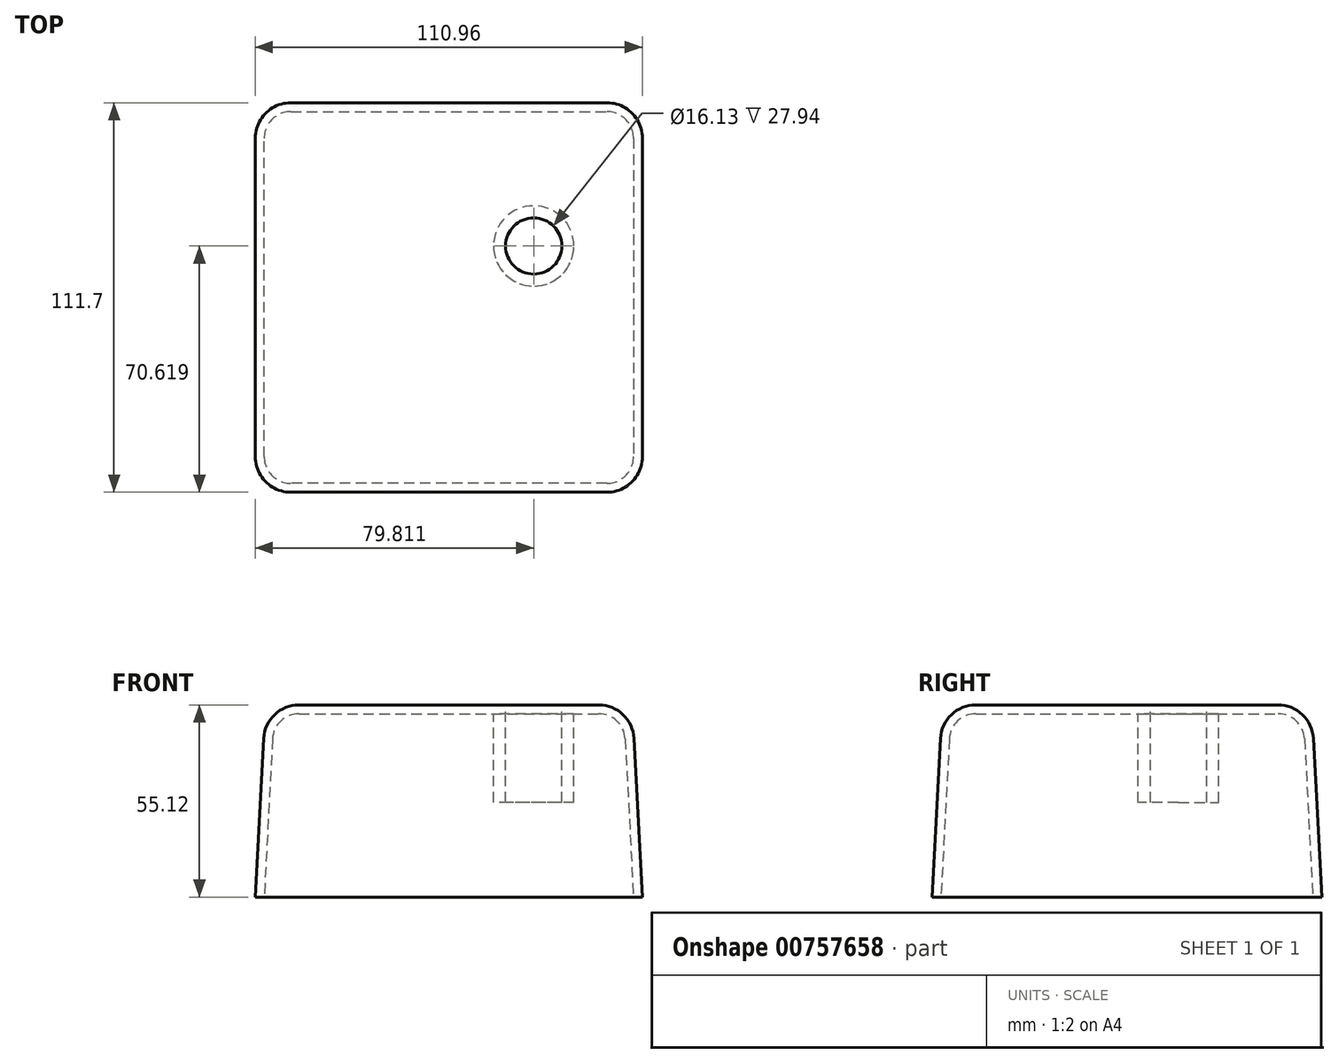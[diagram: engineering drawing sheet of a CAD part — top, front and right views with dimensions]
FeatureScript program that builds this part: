
annotation { "Feature Type Name" : "Feature", "Feature Type Description" : "" }
export const myFeature = defineFeature(function(context is Context, id is Id, definition is map)
    precondition{}
    {
        {
            var Q0;
            Q0=qCreatedBy(makeId("Top.planeOp"),FACE);
            var sketch = newSketch(context, id + "F0", { "sketchPlane" : qUnion([Q0])});
            skLineSegment(sketch, "E0.bottom", {"start": v(55.48, -55.85) * mm, "end": v(-55.48, -55.85) * mm});
            skLineSegment(sketch, "E0.top", {"start": v(55.48, 55.85) * mm, "end": v(-55.48, 55.85) * mm});
            skLineSegment(sketch, "E0.left", {"start": v(55.48, -55.85) * mm, "end": v(55.48, 55.85) * mm});
            skLineSegment(sketch, "E0.right", {"start": v(-55.48, -55.85) * mm, "end": v(-55.48, 55.85) * mm});
            skPoint(sketch, "E0.middle", {"position": v(0, 0) * mm});
            skSolve(sketch);
        }
        {
            var Q0;
            Q0=makeQuery(id+"F0.imprint","IMPRINT",FACE,{"disambiguationData":[TD([[makeQuery(id+"F0.imprint","IMPRINT",EDGE,{"derivedFrom":sQuery(id+"F0.wireOp",EDGE,"E0.bottom")}),-1.0]])]});
            extrude(context, id + "F1", {"entities" : qUnion([Q0]), "depth" : 55.12 * mm, "offsetDistance" : 25.4 * mm, "hasDraft" : true, "draftAngle" : 3 * degree, "draftPullDirection" : true});
        }
        {
            var Q0;
            Q0=makeQuery(id+"F1.opExtrude","SWEPT_EDGE",EDGE,{"disambiguationData":[OSD([sQuery(id+"F0.wireOp",EDGE,"E0.bottom"),sQuery(id+"F0.wireOp",EDGE,"E0.left")])]});
            var Q1;
            Q1=makeQuery(id+"F1.opExtrude","CAP_EDGE",EDGE,{"disambiguationData":[OSD([sQuery(id+"F0.wireOp",EDGE,"E0.left")])],"isStart":false});
            var Q2;
            Q2=makeQuery(id+"F1.opExtrude","CAP_EDGE",EDGE,{"disambiguationData":[OSD([sQuery(id+"F0.wireOp",EDGE,"E0.bottom")])],"isStart":false});
            var Q3;
            Q3=makeQuery(id+"F1.opExtrude","SWEPT_EDGE",EDGE,{"disambiguationData":[OSD([sQuery(id+"F0.wireOp",EDGE,"E0.top"),sQuery(id+"F0.wireOp",EDGE,"E0.left")])]});
            var Q4;
            Q4=makeQuery(id+"F1.opExtrude","CAP_EDGE",EDGE,{"disambiguationData":[OSD([sQuery(id+"F0.wireOp",EDGE,"E0.top")])],"isStart":false});
            var Q5;
            Q5=makeQuery(id+"F1.opExtrude","SWEPT_EDGE",EDGE,{"disambiguationData":[OSD([sQuery(id+"F0.wireOp",EDGE,"E0.top"),sQuery(id+"F0.wireOp",EDGE,"E0.right")])]});
            var Q6;
            Q6=makeQuery(id+"F1.opExtrude","CAP_EDGE",EDGE,{"disambiguationData":[OSD([sQuery(id+"F0.wireOp",EDGE,"E0.right")])],"isStart":false});
            var Q7;
            Q7=makeQuery(id+"F1.opExtrude","SWEPT_EDGE",EDGE,{"disambiguationData":[OSD([sQuery(id+"F0.wireOp",EDGE,"E0.bottom"),sQuery(id+"F0.wireOp",EDGE,"E0.right")])]});
            fillet(context, id + "F2", {"entities" : qUnion([Q0, Q1, Q2, Q3, Q4, Q5, Q6, Q7]), "radius" : 10.16 * mm, "tangentPropagation" : true, "allowEdgeOverflow" : false});
        }
        {
            var Q0;
            Q0=makeQuery(id+"F1.opExtrude","CAP_FACE",FACE,{"disambiguationData":[OSD([sQuery(id+"F0.wireOp",EDGE,"E0.bottom"),sQuery(id+"F0.wireOp",EDGE,"E0.top"),sQuery(id+"F0.wireOp",EDGE,"E0.left"),sQuery(id+"F0.wireOp",EDGE,"E0.right")])],"isStart":true});
            shell(context, id + "F3", {"entities" : qUnion([Q0]), "thickness" : 2.54 * mm});
        }
        {
            var Q0;
            Q0=makeQuery(id+"F3.opShell","OFFSET_FACE",FACE,{"disambiguationData":[OSD([sQuery(id+"F0.wireOp",EDGE,"E0.bottom"),sQuery(id+"F0.wireOp",EDGE,"E0.top"),sQuery(id+"F0.wireOp",EDGE,"E0.left"),sQuery(id+"F0.wireOp",EDGE,"E0.right")])]});
            var sketch = newSketch(context, id + "F4", { "sketchPlane" : qUnion([Q0])});
            skCircle(sketch, "E1", {"center": v(24.33, -14.77) * mm, "radius": 11.52 * mm});
            skCircle(sketch, "E2", {"center": v(24.33, -14.77) * mm, "radius": 8.07 * mm});
            skSolve(sketch);
        }
        {
            var Q0;
            Q0=makeQuery(id+"F4.imprint","IMPRINT",FACE,{"disambiguationData":[TD([[makeQuery(id+"F4.imprint","IMPRINT",EDGE,{"derivedFrom":sQuery(id+"F4.wireOp",EDGE,"E1")}),1.0]])]});
            extrude(context, id + "F5", {"entities" : qUnion([Q0]), "operationType" : NewBodyOperationType.ADD, "depth" : 25.4 * mm, "offsetDistance" : 25.4 * mm});
        }
        {
            var Q0;
            Q0=makeQuery(id+"F5.boolean.opBoolean","SPLIT",FACE,{"disambiguationData":[TD([makeQuery(id+"F5.opExtrude","SWEPT_FACE",FACE,{"disambiguationData":[OSD([sQuery(id+"F4.wireOp",EDGE,"E2")])]})])],"derivedFrom":makeQuery(id+"F3.opShell","OFFSET_FACE",FACE,{"disambiguationData":[OSD([sQuery(id+"F0.wireOp",EDGE,"E0.bottom"),sQuery(id+"F0.wireOp",EDGE,"E0.top"),sQuery(id+"F0.wireOp",EDGE,"E0.left"),sQuery(id+"F0.wireOp",EDGE,"E0.right")])]})});
            extrude(context, id + "F6", {"entities" : qUnion([Q0]), "operationType" : NewBodyOperationType.REMOVE, "oppositeDirection" : true, "depth" : 25.4 * mm, "offsetDistance" : 25.4 * mm});
        }
    });
